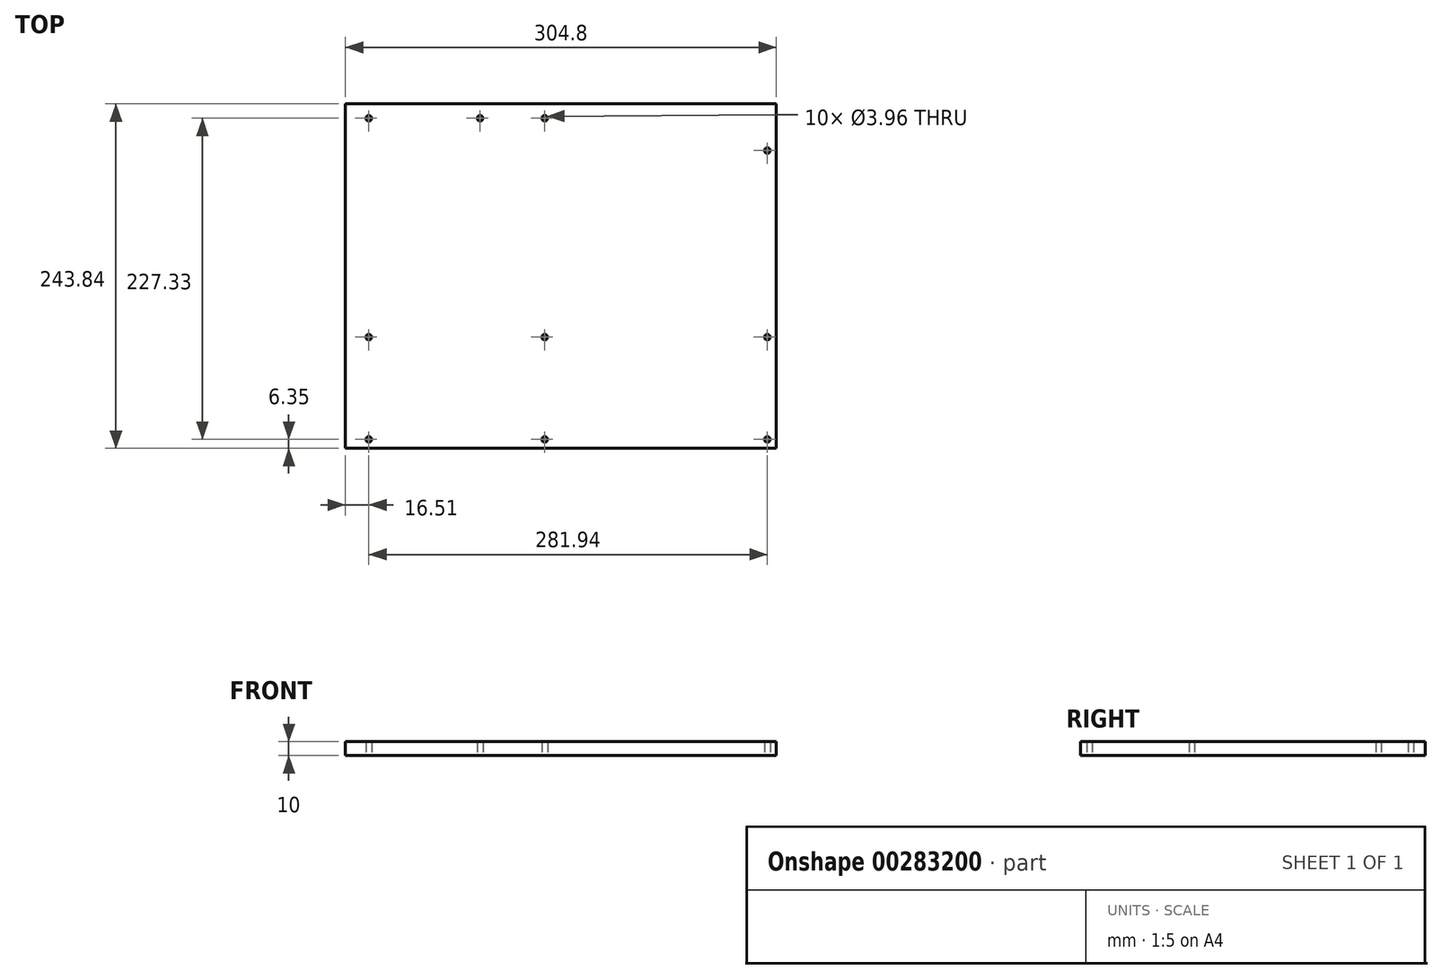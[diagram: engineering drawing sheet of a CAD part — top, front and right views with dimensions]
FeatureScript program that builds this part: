
annotation { "Feature Type Name" : "Feature", "Feature Type Description" : "" }
export const myFeature = defineFeature(function(context is Context, id is Id, definition is map)
    precondition{}
    {
        {
            var Q0;
            Q0=qCreatedBy(makeId("Top.planeOp"),FACE);
            var sketch = newSketch(context, id + "F0", { "sketchPlane" : qUnion([Q0])});
            skLineSegment(sketch, "E0.bottom", {"start": v(152.4, -121.92) * mm, "end": v(-152.4, -121.92) * mm});
            skLineSegment(sketch, "E0.top", {"start": v(152.4, 121.92) * mm, "end": v(-152.4, 121.92) * mm});
            skLineSegment(sketch, "E0.left", {"start": v(152.4, -121.92) * mm, "end": v(152.4, 121.92) * mm});
            skLineSegment(sketch, "E0.right", {"start": v(-152.4, -121.92) * mm, "end": v(-152.4, 121.92) * mm});
            skPoint(sketch, "E0.middle", {"position": v(0, 0) * mm});
            skLineSegment(sketch, "E1", {"start": v(-152.4, 111.76) * mm, "end": v(-135.9, 111.76) * mm, "construction": true});
            skLineSegment(sketch, "E2", {"start": v(-135.9, 111.76) * mm, "end": v(-135.9, 121.92) * mm, "construction": true});
            skLineSegment(sketch, "E3", {"start": v(-135.9, 111.76) * mm, "end": v(-57.15, 111.76) * mm, "construction": true});
            skLineSegment(sketch, "E4", {"start": v(-57.15, 111.76) * mm, "end": v(-11.43, 111.76) * mm, "construction": true});
            skPoint(sketch, "E4.endSnap0", {"position": v(-96.52, 111.76) * mm});
            skLineSegment(sketch, "E5", {"start": v(-135.9, 111.76) * mm, "end": v(-135.9, -43.18) * mm, "construction": true});
            skLineSegment(sketch, "E6", {"start": v(-135.9, 111.76) * mm, "end": v(-135.9, -115.57) * mm, "construction": true});
            skLineSegment(sketch, "E7", {"start": v(-135.9, -43.18) * mm, "end": v(-11.43, -43.18) * mm, "construction": true});
            skLineSegment(sketch, "E8", {"start": v(-135.9, -115.57) * mm, "end": v(-11.43, -115.57) * mm});
            skLineSegment(sketch, "E9", {"start": v(-11.43, -115.57) * mm, "end": v(146.05, -115.57) * mm});
            skLineSegment(sketch, "E10", {"start": v(146.05, -115.57) * mm, "end": v(146.05, -43.18) * mm, "construction": true});
            skLineSegment(sketch, "E11", {"start": v(-11.43, -43.18) * mm, "end": v(146.05, -43.18) * mm, "construction": true});
            skLineSegment(sketch, "E12", {"start": v(146.05, -43.18) * mm, "end": v(146.05, 88.9) * mm, "construction": true});
            skCircle(sketch, "E13", {"center": v(-135.9, 111.76) * mm, "radius": 1.98 * mm});
            skCircle(sketch, "E14", {"center": v(-135.9, -43.18) * mm, "radius": 1.98 * mm});
            skCircle(sketch, "E15", {"center": v(-57.15, 111.76) * mm, "radius": 1.98 * mm});
            skCircle(sketch, "E16", {"center": v(-11.43, 111.76) * mm, "radius": 1.98 * mm});
            skCircle(sketch, "E17", {"center": v(-11.43, -43.18) * mm, "radius": 1.98 * mm});
            skCircle(sketch, "E18", {"center": v(146.05, -43.18) * mm, "radius": 1.98 * mm});
            skCircle(sketch, "E19", {"center": v(146.05, 88.9) * mm, "radius": 1.98 * mm});
            skCircle(sketch, "E20", {"center": v(-135.9, -115.57) * mm, "radius": 1.98 * mm});
            skCircle(sketch, "E21", {"center": v(-11.43, -115.57) * mm, "radius": 1.98 * mm});
            skCircle(sketch, "E22", {"center": v(146.05, -115.57) * mm, "radius": 1.98 * mm});
            skLineSegment(sketch, "E23", {"start": v(-11.43, -43.18) * mm, "end": v(-11.43, -115.57) * mm, "construction": true});
            skLineSegment(sketch, "E24.bottom", {"start": v(-177.8, 147.32) * mm, "end": v(177.8, 147.32) * mm});
            skLineSegment(sketch, "E24.top", {"start": v(-177.8, -147.32) * mm, "end": v(177.8, -147.32) * mm});
            skLineSegment(sketch, "E24.left", {"start": v(-177.8, 147.32) * mm, "end": v(-177.8, -147.32) * mm});
            skLineSegment(sketch, "E24.right", {"start": v(177.8, 147.32) * mm, "end": v(177.8, -147.32) * mm});
            skLineSegment(sketch, "E25", {"start": v(-135.9, 121.92) * mm, "end": v(-135.9, 147.32) * mm});
            skLineSegment(sketch, "E26", {"start": v(-152.4, -121.92) * mm, "end": v(-152.4, -147.32) * mm, "construction": true});
            skSolve(sketch);
        }
        {
            var Q0;
            Q0=makeQuery(id+"F0.imprint","IMPRINT",FACE,{"disambiguationData":[TD([[makeQuery(id+"F0.imprint","IMPRINT",EDGE,{"derivedFrom":sQuery(id+"F0.wireOp",EDGE,"E0.bottom")}),-1.0]])]});
            extrude(context, id + "F1", {"entities" : qUnion([Q0]), "depth" : 10 * mm});
        }
    });
